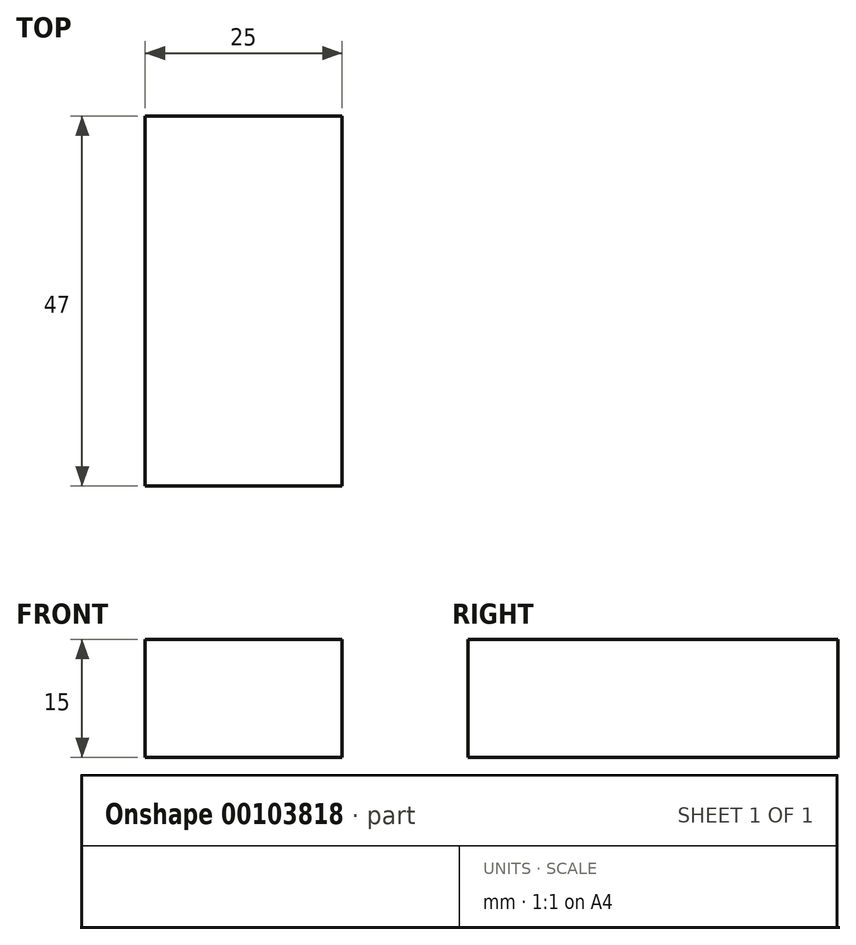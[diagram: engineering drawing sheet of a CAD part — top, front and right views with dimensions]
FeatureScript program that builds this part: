
annotation { "Feature Type Name" : "Feature", "Feature Type Description" : "" }
export const myFeature = defineFeature(function(context is Context, id is Id, definition is map)
    precondition{}
    {
        {
            var Q0;
            Q0=qCreatedBy(makeId("Front.planeOp"),FACE);
            var sketch = newSketch(context, id + "F0", { "sketchPlane" : qUnion([Q0])});
            skLineSegment(sketch, "E0.bottom", {"start": v(-94.08, -44.95) * mm, "end": v(-69.08, -44.95) * mm});
            skLineSegment(sketch, "E0.top", {"start": v(-94.08, -59.95) * mm, "end": v(-69.08, -59.95) * mm});
            skLineSegment(sketch, "E0.left", {"start": v(-94.08, -44.95) * mm, "end": v(-94.08, -59.95) * mm});
            skLineSegment(sketch, "E0.right", {"start": v(-69.08, -44.95) * mm, "end": v(-69.08, -59.95) * mm});
            skSolve(sketch);
        }
        {
            var Q0;
            Q0=makeQuery(id+"F0.imprint","IMPRINT",FACE,{"disambiguationData":[TD([[makeQuery(id+"F0.imprint","IMPRINT",EDGE,{"derivedFrom":sQuery(id+"F0.wireOp",EDGE,"E0.bottom")}),-1.0]])]});
            extrude(context, id + "F1", {"entities" : qUnion([Q0]), "depth" : 47 * mm});
        }
    });
